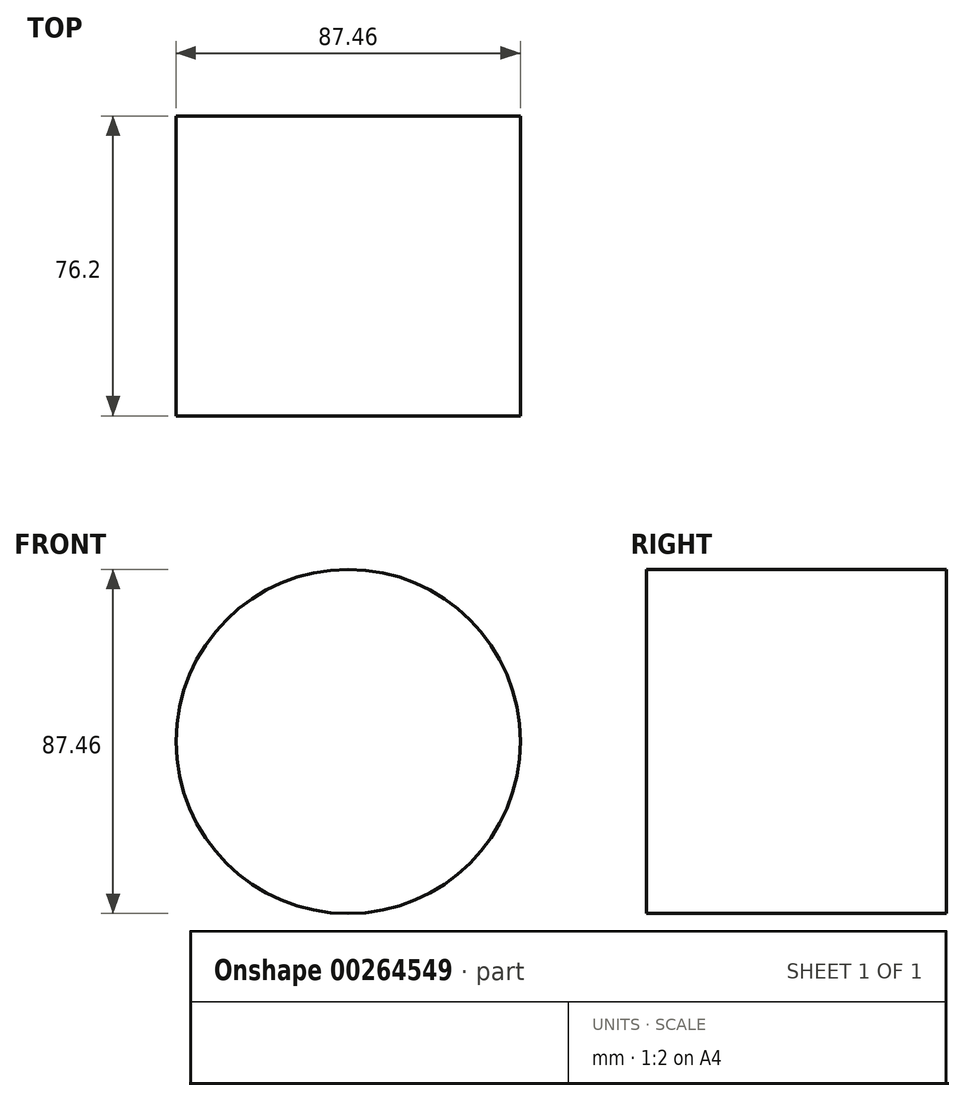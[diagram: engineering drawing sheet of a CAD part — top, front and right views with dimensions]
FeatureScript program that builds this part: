
annotation { "Feature Type Name" : "Feature", "Feature Type Description" : "" }
export const myFeature = defineFeature(function(context is Context, id is Id, definition is map)
    precondition{}
    {
        {
            var Q0;
            Q0=qCreatedBy(makeId("Front.planeOp"),FACE);
            var sketch = newSketch(context, id + "F0", { "sketchPlane" : qUnion([Q0])});
            skCircle(sketch, "E0", {"center": v(0, 0) * mm, "radius": 43.73 * mm});
            skSolve(sketch);
        }
        {
            var Q0;
            Q0 = qSketchRegion(id + "F0", true);
            extrude(context, id + "F1", {"entities" : qUnion([Q0]), "depth" : 76.2 * mm});
        }
    });
